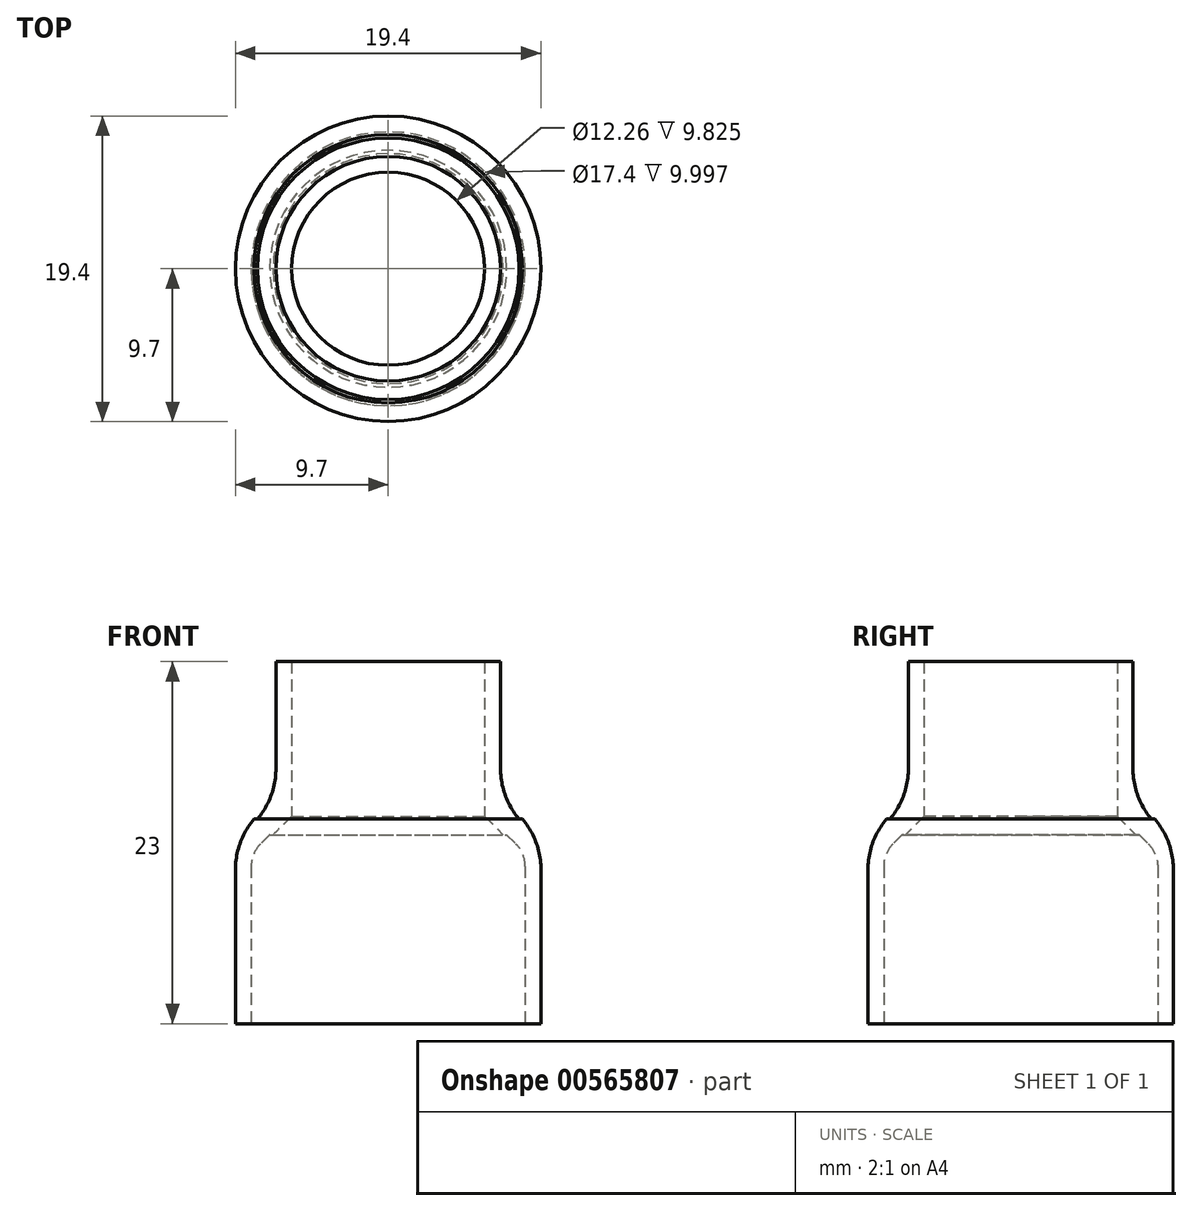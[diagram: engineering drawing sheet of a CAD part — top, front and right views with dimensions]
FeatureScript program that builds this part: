
annotation { "Feature Type Name" : "Feature", "Feature Type Description" : "" }
export const myFeature = defineFeature(function(context is Context, id is Id, definition is map)
    precondition{}
    {
        {
            var Q0;
            Q0=qCreatedBy(makeId("Front.planeOp"),FACE);
            var sketch = newSketch(context, id + "F0", { "sketchPlane" : qUnion([Q0])});
            skLineSegment(sketch, "E0.bottom", {"start": v(0, 0) * mm, "end": v(-7.13, 0) * mm});
            skLineSegment(sketch, "E0.top", {"start": v(0, 13) * mm, "end": v(-7.13, 13) * mm});
            skLineSegment(sketch, "E0.left", {"start": v(0, 0) * mm, "end": v(0, 13) * mm});
            skLineSegment(sketch, "E0.right", {"start": v(-7.13, 0) * mm, "end": v(-7.13, 13) * mm});
            skLineSegment(sketch, "E1.bottom", {"start": v(0, 3) * mm, "end": v(-9.7, 3) * mm});
            skLineSegment(sketch, "E1.top", {"start": v(0, -10) * mm, "end": v(-9.7, -10) * mm});
            skLineSegment(sketch, "E1.left", {"start": v(0, 3) * mm, "end": v(0, -10) * mm});
            skLineSegment(sketch, "E1.right", {"start": v(-9.7, 3) * mm, "end": v(-9.7, -10) * mm});
            skSolve(sketch);
        }
        {
            var Q0;
            {var subQ0=sQuery(id+"F0.wireOp",EDGE,"E0.top");Q0=makeQuery(id+"F0.imprint","IMPRINT",FACE,{"disambiguationData":[TD([[makeQuery(id+"F0.imprint","IMPRINT",EDGE,{"derivedFrom":subQ0}),1.0]])]});}
            var Q1;
            {var subQ0=sQuery(id+"F0.wireOp",EDGE,"E0.bottom");Q1=makeQuery(id+"F0.imprint","IMPRINT",FACE,{"disambiguationData":[TD([[makeQuery(id+"F0.imprint","IMPRINT",EDGE,{"derivedFrom":subQ0}),-1.0]])]});}
            var Q2;
            {var subQ5=sQuery(id+"F0.wireOp",EDGE,"E0.bottom");Q2=makeQuery(id+"F0.imprint","IMPRINT",FACE,{"disambiguationData":[TD([[makeQuery(id+"F0.imprint","IMPRINT",EDGE,{"derivedFrom":subQ5}),1.0]])]});}
            var Q3;
            Q3=sQuery(id+"F0.wireOp",EDGE,"E0.left");
            revolve(context, id + "F1", {"entities" : qUnion([Q0, Q1, Q2]), "axis" : qUnion([Q3]), "revolveType" : RevolveType.FULL});
        }
        {
            var Q0;
            Q0=makeQuery(id+"F1.opRevolve","SWEPT_FACE",FACE,{"disambiguationData":[OSD([sQuery(id+"F0.wireOp",EDGE,"E0.top")])]});
            var Q1;
            Q1=makeQuery(id+"F1.opRevolve","SWEPT_FACE",FACE,{"disambiguationData":[OSD([sQuery(id+"F0.wireOp",EDGE,"E1.top")])]});
            shell(context, id + "F2", {"entities" : qUnion([Q0, Q1]), "thickness" : 1 * mm});
        }
        {
            var Q0;
            Q0=makeQuery(id+"F2.opShell","OFFSET_EDGE",EDGE,{"disambiguationData":[OSD([sQuery(id+"F0.wireOp",EDGE,"E0.right"),sQuery(id+"F0.wireOp",EDGE,"E1.bottom")])]});
            var Q1;
            Q1=makeQuery(id+"F2.opShell","OFFSET_FACE",FACE,{"disambiguationData":[OSD([sQuery(id+"F0.wireOp",EDGE,"E1.bottom")])]});
            chamfer(context, id + "F3", {"entities" : qUnion([Q0, Q1]), "width" : 1.18 * mm, "tangentPropagation" : true});
        }
        {
            var Q0;
            Q0=makeQuery(id+"F1.opRevolve","SWEPT_EDGE",EDGE,{"disambiguationData":[OSD([sQuery(id+"F0.wireOp",EDGE,"E1.bottom"),sQuery(id+"F0.wireOp",EDGE,"E1.right")])]});
            var Q1;
            Q1=makeQuery(id+"F1.opRevolve","SWEPT_EDGE",EDGE,{"disambiguationData":[OSD([sQuery(id+"F0.wireOp",EDGE,"E0.right"),sQuery(id+"F0.wireOp",EDGE,"E1.bottom")])]});
            chamfer(context, id + "F4", {"entities" : qUnion([Q0, Q1]), "width" : 1.18 * mm, "tangentPropagation" : true});
        }
        {
            var Q0;
            {var subQ0=sQuery(id+"F0.wireOp",EDGE,"E1.right");Q0=makeQuery(id+"F3.opChamfer","BLEND_EDGE",EDGE,{"blendedFrom":[makeQuery(id+"F2.opShell","OFFSET_EDGE",EDGE,{"disambiguationData":[OSD([sQuery(id+"F0.wireOp",EDGE,"E1.bottom"),subQ0])]}),makeQuery(id+"F2.opShell","OFFSET_FACE",FACE,{"disambiguationData":[OSD([subQ0])]})],"blendedInto":[makeQuery(id+"F2.opShell","OFFSET_FACE",FACE,{"disambiguationData":[OSD([subQ0])]})]});}
            fillet(context, id + "F5", {"entities" : qUnion([Q0]), "radius" : 2 * mm, "tangentPropagation" : true, "allowEdgeOverflow" : false});
        }
        {
            var Q0;
            {var subQ0=sQuery(id+"F0.wireOp",EDGE,"E0.right");Q0=makeQuery(id+"F4.opChamfer","BLEND_EDGE",EDGE,{"blendedFrom":[makeQuery(id+"F1.opRevolve","SWEPT_EDGE",EDGE,{"disambiguationData":[OSD([subQ0,sQuery(id+"F0.wireOp",EDGE,"E1.bottom")])]}),makeQuery(id+"F1.opRevolve","SWEPT_FACE",FACE,{"disambiguationData":[OSD([subQ0])]})],"blendedInto":[makeQuery(id+"F1.opRevolve","SWEPT_FACE",FACE,{"disambiguationData":[OSD([subQ0])]})]});}
            fillet(context, id + "F6", {"entities" : qUnion([Q0]), "radius" : 5 * mm, "tangentPropagation" : true, "allowEdgeOverflow" : false});
        }
        {
            var Q0;
            {var subQ0=sQuery(id+"F0.wireOp",EDGE,"E1.right");Q0=makeQuery(id+"F4.opChamfer","BLEND_EDGE",EDGE,{"blendedFrom":[makeQuery(id+"F1.opRevolve","SWEPT_EDGE",EDGE,{"disambiguationData":[OSD([sQuery(id+"F0.wireOp",EDGE,"E1.bottom"),subQ0])]}),makeQuery(id+"F1.opRevolve","SWEPT_FACE",FACE,{"disambiguationData":[OSD([subQ0])]})],"blendedInto":[makeQuery(id+"F1.opRevolve","SWEPT_FACE",FACE,{"disambiguationData":[OSD([subQ0])]})]});}
            fillet(context, id + "F7", {"entities" : qUnion([Q0]), "radius" : 5 * mm, "tangentPropagation" : true, "allowEdgeOverflow" : false});
        }
    });
